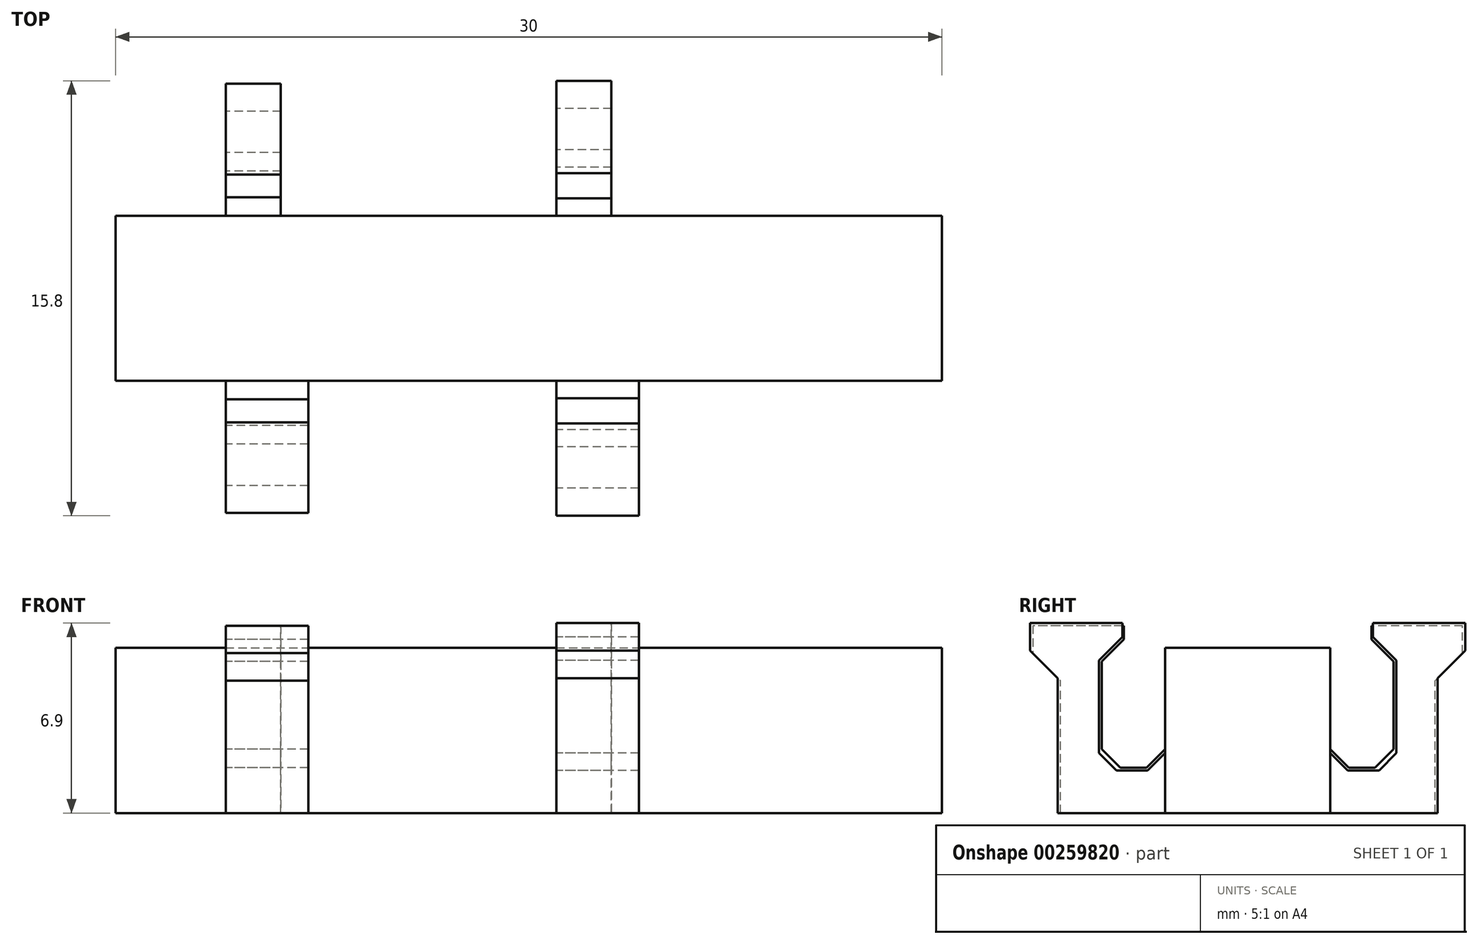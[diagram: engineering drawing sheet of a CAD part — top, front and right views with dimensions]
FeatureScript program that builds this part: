
annotation { "Feature Type Name" : "Feature", "Feature Type Description" : "" }
export const myFeature = defineFeature(function(context is Context, id is Id, definition is map)
    precondition{}
    {
        {
            var Q0;
            Q0=qCreatedBy(makeId("Top.planeOp"),FACE);
            var sketch = newSketch(context, id + "F0", { "sketchPlane" : qUnion([Q0])});
            skLineSegment(sketch, "E0.bottom", {"start": v(0, 0) * mm, "end": v(30, 0) * mm});
            skLineSegment(sketch, "E0.top", {"start": v(0, 6) * mm, "end": v(30, 6) * mm});
            skLineSegment(sketch, "E0.left", {"start": v(0, 0) * mm, "end": v(0, 6) * mm});
            skLineSegment(sketch, "E0.right", {"start": v(30, 0) * mm, "end": v(30, 6) * mm});
            skSolve(sketch);
        }
        {
            var Q0;
            Q0 = qSketchRegion(id + "F0", true);
            extrude(context, id + "F1", {"entities" : qUnion([Q0]), "depth" : 6 * mm});
        }
        {
            var Q0;
            Q0=qCreatedBy(makeId("Right.planeOp"),FACE);
            var sketch = newSketch(context, id + "F2", { "sketchPlane" : qUnion([Q0])});
            skCircle(sketch, "E1", {"center": v(-1.15, 2.8) * mm, "radius": 1.05 * mm, "construction": true});
            skCircle(sketch, "E2", {"center": v(-1.15, 5.03) * mm, "radius": 1.05 * mm, "construction": true});
            skPoint(sketch, "E3", {"position": v(-1.15, 6.08) * mm});
            skPoint(sketch, "E4", {"position": v(-1.15, 1.75) * mm});
            skArc(sketch, "E5", {"start": v(-0.48, 3.6) * mm, "mid": v(-0.62, 3.92) * mm, "end": v(-0.48, 4.22) * mm, "construction": true});
            skArc(sketch, "E6", {"start": v(-1.82, 3.6) * mm, "mid": v(-1.68, 3.92) * mm, "end": v(-1.82, 4.22) * mm, "construction": true});
            skPoint(sketch, "E7", {"position": v(-0.1, 2.8) * mm});
            skPoint(sketch, "E8", {"position": v(-2.2, 5.03) * mm});
            skSolve(sketch);
        }
        {
            var Q0;
            Q0=makeQuery(id+"F1.opExtrude","SWEPT_FACE",FACE,{"disambiguationData":[OSD([sQuery(id+"F0.wireOp",EDGE,"E0.left")])]});
            cPlane(context, id + "F3", {"entities" : qUnion([Q0]), "cplaneType" : CPlaneType.OFFSET, "offset" : 4 * mm, "oppositeDirection" : true, "width" : 150 * mm, "height" : 150 * mm});
        }
        {
            var Q0;
            Q0=qCreatedBy(id+"F3.planeOp",FACE);
            var sketch = newSketch(context, id + "F4", { "sketchPlane" : qUnion([Q0])});
            skLineSegment(sketch, "E9", {"start": v(0, 0) * mm, "end": v(3.8, 0) * mm});
            skLineSegment(sketch, "E10", {"start": v(3.8, 0) * mm, "end": v(3.8, 4.8) * mm});
            skLineSegment(sketch, "E11", {"start": v(0, 0) * mm, "end": v(0, 2.32) * mm});
            skLineSegment(sketch, "E12", {"start": v(0, 2.32) * mm, "end": v(0.67, 1.65) * mm});
            skLineSegment(sketch, "E13", {"start": v(0.67, 1.65) * mm, "end": v(1.63, 1.65) * mm});
            skLineSegment(sketch, "E14", {"start": v(1.63, 1.65) * mm, "end": v(2.3, 2.32) * mm});
            skLineSegment(sketch, "E15", {"start": v(2.3, 2.32) * mm, "end": v(2.3, 5.5) * mm});
            skLineSegment(sketch, "E16", {"start": v(2.3, 5.5) * mm, "end": v(1.5, 6.3) * mm});
            skLineSegment(sketch, "E17", {"start": v(1.5, 6.3) * mm, "end": v(1.5, 6.8) * mm});
            skLineSegment(sketch, "E18", {"start": v(1.5, 6.8) * mm, "end": v(4.8, 6.8) * mm});
            skLineSegment(sketch, "E19", {"start": v(4.8, 6.8) * mm, "end": v(4.8, 5.8) * mm});
            skLineSegment(sketch, "E20", {"start": v(4.8, 5.8) * mm, "end": v(3.8, 4.8) * mm});
            skLineSegment(sketch, "E21", {"start": v(0.34, 1.99) * mm, "end": v(0.4, 2.06) * mm, "construction": true});
            skLineSegment(sketch, "E22", {"start": v(1.15, 1.65) * mm, "end": v(1.15, 1.75) * mm, "construction": true});
            skLineSegment(sketch, "E23", {"start": v(1.96, 5.84) * mm, "end": v(1.9, 5.77) * mm, "construction": true});
            skSolve(sketch);
        }
        {
            var Q0;
            Q0 = qSketchRegion(id + "F4", true);
            extrude(context, id + "F5", {"entities" : qUnion([Q0]), "operationType" : NewBodyOperationType.ADD, "oppositeDirection" : true, "depth" : 3 * mm});
        }
        {
            var Q0;
            Q0=qCreatedBy(id+"F3.planeOp",FACE);
            var sketch = newSketch(context, id + "F6", { "sketchPlane" : qUnion([Q0])});
            skLineSegment(sketch, "E24.0.0", {"start": v(3.8, 4.8) * mm, "end": v(4.8, 5.8) * mm, "construction": true});
            skLineSegment(sketch, "E24.0.1", {"start": v(4.8, 5.8) * mm, "end": v(4.8, 6.8) * mm, "construction": true});
            skLineSegment(sketch, "E24.0.2", {"start": v(4.8, 6.8) * mm, "end": v(1.5, 6.8) * mm, "construction": true});
            skLineSegment(sketch, "E24.0.3", {"start": v(1.5, 6.8) * mm, "end": v(1.5, 6.3) * mm, "construction": true});
            skLineSegment(sketch, "E24.0.4", {"start": v(1.5, 6.3) * mm, "end": v(2.3, 5.5) * mm, "construction": true});
            skLineSegment(sketch, "E24.0.5", {"start": v(2.3, 5.5) * mm, "end": v(2.3, 2.32) * mm, "construction": true});
            skLineSegment(sketch, "E24.0.6", {"start": v(2.3, 2.32) * mm, "end": v(1.63, 1.65) * mm, "construction": true});
            skLineSegment(sketch, "E24.0.7", {"start": v(1.63, 1.65) * mm, "end": v(0.67, 1.65) * mm, "construction": true});
            skLineSegment(sketch, "E24.0.8", {"start": v(0.67, 1.65) * mm, "end": v(0, 2.32) * mm, "construction": true});
            skLineSegment(sketch, "E24.0.9", {"start": v(0, 2.32) * mm, "end": v(0, 0) * mm, "construction": true});
            skLineSegment(sketch, "E24.0.10", {"start": v(0, 0) * mm, "end": v(3.8, 0) * mm, "construction": true});
            skLineSegment(sketch, "E24.0.11", {"start": v(3.8, 0) * mm, "end": v(3.8, 4.8) * mm, "construction": true});
            skLineSegment(sketch, "E25", {"start": v(-3, 0) * mm, "end": v(-3, 6) * mm, "construction": true});
            skLineSegment(sketch, "E26.MirrorCS", {"start": v(-7.5, 6.8) * mm, "end": v(-7.5, 6.3) * mm});
            skLineSegment(sketch, "E27.MirrorCS", {"start": v(-6, 0) * mm, "end": v(-9.8, 0) * mm});
            skLineSegment(sketch, "E28.MirrorCS", {"start": v(-8.3, 2.32) * mm, "end": v(-7.63, 1.65) * mm});
            skLineSegment(sketch, "E29.MirrorCS", {"start": v(-9.8, 0) * mm, "end": v(-9.8, 4.8) * mm});
            skLineSegment(sketch, "E30.MirrorCS", {"start": v(-6, 2.32) * mm, "end": v(-6, 0) * mm});
            skLineSegment(sketch, "E31.MirrorCS", {"start": v(-6.67, 1.65) * mm, "end": v(-6, 2.32) * mm});
            skLineSegment(sketch, "E32.MirrorCS", {"start": v(-7.63, 1.65) * mm, "end": v(-6.67, 1.65) * mm});
            skLineSegment(sketch, "E33.MirrorCS", {"start": v(-8.3, 5.5) * mm, "end": v(-8.3, 2.32) * mm});
            skLineSegment(sketch, "E34.MirrorCS", {"start": v(-7.5, 6.3) * mm, "end": v(-8.3, 5.5) * mm});
            skLineSegment(sketch, "E35.MirrorCS", {"start": v(-10.8, 6.8) * mm, "end": v(-7.5, 6.8) * mm});
            skLineSegment(sketch, "E36.MirrorCS", {"start": v(-9.8, 4.8) * mm, "end": v(-10.8, 5.8) * mm});
            skLineSegment(sketch, "E37.MirrorCS", {"start": v(-10.8, 5.8) * mm, "end": v(-10.8, 6.8) * mm});
            skSolve(sketch);
        }
        {
            var Q0;
            Q0 = qSketchRegion(id + "F6", true);
            extrude(context, id + "F7", {"entities" : qUnion([Q0]), "operationType" : NewBodyOperationType.ADD, "oppositeDirection" : true, "depth" : 2 * mm});
        }
        {
            var Q0;
            Q0=makeQuery(id+"F1.opExtrude","SWEPT_FACE",FACE,{"disambiguationData":[OSD([sQuery(id+"F0.wireOp",EDGE,"E0.left")])]});
            cPlane(context, id + "F8", {"entities" : qUnion([Q0]), "cplaneType" : CPlaneType.OFFSET, "offset" : 16 * mm, "oppositeDirection" : true, "width" : 150 * mm, "height" : 150 * mm});
        }
        {
            var Q0;
            Q0=qCreatedBy(id+"F8.planeOp",FACE);
            var sketch = newSketch(context, id + "F9", { "sketchPlane" : qUnion([Q0])});
            skLineSegment(sketch, "E38", {"start": v(0, 0) * mm, "end": v(3.9, 0) * mm});
            skLineSegment(sketch, "E39", {"start": v(3.9, 0) * mm, "end": v(3.9, 4.9) * mm});
            skLineSegment(sketch, "E40", {"start": v(0, 0) * mm, "end": v(0, 2.18) * mm});
            skLineSegment(sketch, "E41", {"start": v(0, 2.18) * mm, "end": v(0.63, 1.55) * mm});
            skLineSegment(sketch, "E42", {"start": v(0.63, 1.55) * mm, "end": v(1.77, 1.55) * mm});
            skLineSegment(sketch, "E43", {"start": v(1.77, 1.55) * mm, "end": v(2.4, 2.18) * mm});
            skLineSegment(sketch, "E44", {"start": v(2.4, 2.18) * mm, "end": v(2.4, 5.55) * mm});
            skLineSegment(sketch, "E45", {"start": v(2.4, 5.55) * mm, "end": v(1.55, 6.4) * mm});
            skLineSegment(sketch, "E46", {"start": v(1.55, 6.4) * mm, "end": v(1.55, 6.9) * mm});
            skLineSegment(sketch, "E47", {"start": v(1.55, 6.9) * mm, "end": v(4.9, 6.9) * mm});
            skLineSegment(sketch, "E48", {"start": v(4.9, 6.9) * mm, "end": v(4.9, 5.9) * mm});
            skLineSegment(sketch, "E49", {"start": v(4.9, 5.9) * mm, "end": v(3.9, 4.9) * mm});
            skLineSegment(sketch, "E50", {"start": v(0.27, 1.92) * mm, "end": v(0.4, 2.06) * mm, "construction": true});
            skLineSegment(sketch, "E51", {"start": v(1.15, 1.55) * mm, "end": v(1.15, 1.75) * mm, "construction": true});
            skLineSegment(sketch, "E52", {"start": v(2.03, 5.91) * mm, "end": v(1.9, 5.77) * mm, "construction": true});
            skLineSegment(sketch, "E53", {"start": v(2.4, 5.03) * mm, "end": v(2.2, 5.03) * mm, "construction": true});
            skSolve(sketch);
        }
        {
            var Q0;
            Q0 = qSketchRegion(id + "F9", true);
            extrude(context, id + "F10", {"entities" : qUnion([Q0]), "operationType" : NewBodyOperationType.ADD, "oppositeDirection" : true, "depth" : 3 * mm});
        }
        {
            var Q0;
            Q0=qCreatedBy(id+"F8.planeOp",FACE);
            var sketch = newSketch(context, id + "F11", { "sketchPlane" : qUnion([Q0])});
            skLineSegment(sketch, "E54.0.0", {"start": v(3.9, 4.9) * mm, "end": v(4.9, 5.9) * mm});
            skLineSegment(sketch, "E54.0.1", {"start": v(4.9, 5.9) * mm, "end": v(4.9, 6.9) * mm});
            skLineSegment(sketch, "E54.0.2", {"start": v(4.9, 6.9) * mm, "end": v(1.55, 6.9) * mm});
            skLineSegment(sketch, "E54.0.3", {"start": v(1.55, 6.9) * mm, "end": v(1.55, 6.4) * mm});
            skLineSegment(sketch, "E54.0.4", {"start": v(1.55, 6.4) * mm, "end": v(2.4, 5.55) * mm});
            skLineSegment(sketch, "E54.0.5", {"start": v(2.4, 5.55) * mm, "end": v(2.4, 2.18) * mm});
            skLineSegment(sketch, "E54.0.6", {"start": v(2.4, 2.18) * mm, "end": v(1.77, 1.55) * mm});
            skLineSegment(sketch, "E54.0.7", {"start": v(1.77, 1.55) * mm, "end": v(0.63, 1.55) * mm});
            skLineSegment(sketch, "E54.0.8", {"start": v(0.63, 1.55) * mm, "end": v(0, 2.18) * mm});
            skLineSegment(sketch, "E54.0.9", {"start": v(0, 2.18) * mm, "end": v(0, 0) * mm});
            skLineSegment(sketch, "E54.0.10", {"start": v(0, 0) * mm, "end": v(3.9, 0) * mm});
            skLineSegment(sketch, "E54.0.11", {"start": v(3.9, 0) * mm, "end": v(3.9, 4.9) * mm});
            skLineSegment(sketch, "E55", {"start": v(-3, 6) * mm, "end": v(-3, 0) * mm, "construction": true});
            skLineSegment(sketch, "E56.MirrorCS", {"start": v(-7.55, 6.9) * mm, "end": v(-7.55, 6.4) * mm});
            skLineSegment(sketch, "E57.MirrorCS", {"start": v(-8.4, 5.55) * mm, "end": v(-8.4, 2.18) * mm});
            skLineSegment(sketch, "E58.MirrorCS", {"start": v(-8.4, 2.18) * mm, "end": v(-7.77, 1.55) * mm});
            skLineSegment(sketch, "E59.MirrorCS", {"start": v(-7.77, 1.55) * mm, "end": v(-6.63, 1.55) * mm});
            skLineSegment(sketch, "E60.MirrorCS", {"start": v(-10.9, 6.9) * mm, "end": v(-7.55, 6.9) * mm});
            skLineSegment(sketch, "E61.MirrorCS", {"start": v(-10.9, 5.9) * mm, "end": v(-10.9, 6.9) * mm});
            skLineSegment(sketch, "E62.MirrorCS", {"start": v(-9.9, 4.9) * mm, "end": v(-10.9, 5.9) * mm});
            skLineSegment(sketch, "E63.MirrorCS", {"start": v(-7.55, 6.4) * mm, "end": v(-8.4, 5.55) * mm});
            skLineSegment(sketch, "E64.MirrorCS", {"start": v(-9.9, 0) * mm, "end": v(-9.9, 4.9) * mm});
            skLineSegment(sketch, "E65.MirrorCS", {"start": v(-6, 0) * mm, "end": v(-9.9, 0) * mm});
            skLineSegment(sketch, "E66.MirrorCS", {"start": v(-6.63, 1.55) * mm, "end": v(-6, 2.18) * mm});
            skLineSegment(sketch, "E67.MirrorCS", {"start": v(-6, 2.18) * mm, "end": v(-6, 0) * mm});
            skSolve(sketch);
        }
        {
            var Q0;
            Q0 = qSketchRegion(id + "F11", true);
            extrude(context, id + "F12", {"entities" : qUnion([Q0]), "operationType" : NewBodyOperationType.ADD, "oppositeDirection" : true, "depth" : 2 * mm});
        }
    });
